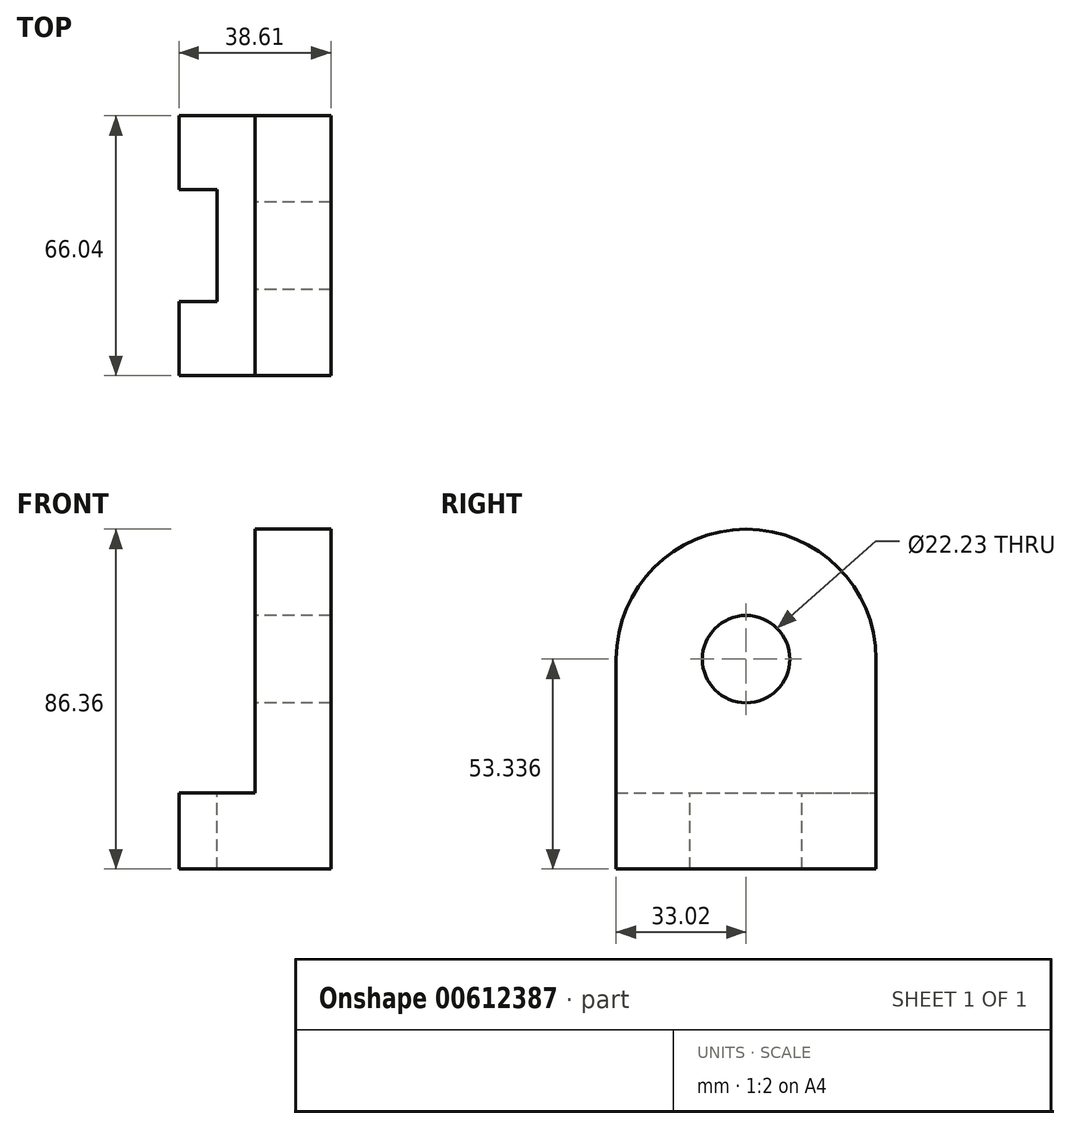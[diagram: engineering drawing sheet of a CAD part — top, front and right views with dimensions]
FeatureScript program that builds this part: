
annotation { "Feature Type Name" : "Feature", "Feature Type Description" : "" }
export const myFeature = defineFeature(function(context is Context, id is Id, definition is map)
    precondition{}
    {
        {
            var Q0;
            Q0=qCreatedBy(makeId("Front.planeOp"),FACE);
            var sketch = newSketch(context, id + "F0", { "sketchPlane" : qUnion([Q0])});
            skLineSegment(sketch, "E0", {"start": v(0, 0) * mm, "end": v(0, -19.3) * mm});
            skLineSegment(sketch, "E1", {"start": v(0, -19.3) * mm, "end": v(38.6, -19.3) * mm});
            skLineSegment(sketch, "E2", {"start": v(38.6, -19.3) * mm, "end": v(38.6, 67.06) * mm});
            skLineSegment(sketch, "E3", {"start": v(38.6, 67.06) * mm, "end": v(19.3, 67.06) * mm});
            skLineSegment(sketch, "E4", {"start": v(19.3, 67.06) * mm, "end": v(19.3, 0) * mm});
            skLineSegment(sketch, "E5", {"start": v(19.3, 0) * mm, "end": v(0, 0) * mm});
            skSolve(sketch);
        }
        {
            var Q0;
            Q0=makeQuery(id+"F0.imprint","IMPRINT",FACE,{"disambiguationData":[TD([[makeQuery(id+"F0.imprint","IMPRINT",EDGE,{"derivedFrom":sQuery(id+"F0.wireOp",EDGE,"E0")}),1.0]])]});
            extrude(context, id + "F1", {"entities" : qUnion([Q0]), "depth" : 66.04 * mm, "offsetDistance" : 25.4 * mm});
        }
        {
            var Q0;
            Q0=makeQuery(id+"F1.opExtrude","CAP_EDGE",EDGE,{"disambiguationData":[OSD([sQuery(id+"F0.wireOp",EDGE,"E3")])],"isStart":true});
            var Q1;
            Q1=makeQuery(id+"F1.opExtrude","CAP_EDGE",EDGE,{"disambiguationData":[OSD([sQuery(id+"F0.wireOp",EDGE,"E3")])],"isStart":false});
            fillet(context, id + "F2", {"entities" : qUnion([Q0, Q1]), "radius" : 33.02 * mm, "tangentPropagation" : true, "allowEdgeOverflow" : false});
        }
        {
            var Q0;
            Q0=makeQuery(id+"F1.opExtrude","SWEPT_FACE",FACE,{"disambiguationData":[OSD([sQuery(id+"F0.wireOp",EDGE,"E4")])]});
            var sketch = newSketch(context, id + "F3", { "sketchPlane" : qUnion([Q0])});
            skCircle(sketch, "E6", {"center": v(33.02, 34.04) * mm, "radius": 11.11 * mm});
            skSolve(sketch);
        }
        {
            var Q0;
            Q0=sQuery(id+"F3.wireOp",VERTEX,"E6.center");
            var Q1;
            Q1=makeQuery(id+"F1.opExtrude","SWEPT_BODY",BODY,{"disambiguationData":[OSD([sQuery(id+"F0.wireOp",EDGE,"E0"),sQuery(id+"F0.wireOp",EDGE,"E1"),sQuery(id+"F0.wireOp",EDGE,"E2"),sQuery(id+"F0.wireOp",EDGE,"E3"),sQuery(id+"F0.wireOp",EDGE,"E4"),sQuery(id+"F0.wireOp",EDGE,"E5")])]});
            hole(context, id + "F4", {"style" : HoleStyle.SIMPLE, "endStyle" : HoleEndStyle.BLIND, "holeDiameter" : 22.22 * mm, "majorDiameter" : 6.35 * mm, "holeDepth" : 50.8 * mm, "isTappedThrough" : true, "tappedDepth" : 12.7 * mm, "tapClearance" : 3, "locations" : qUnion([Q0]), "scope" : qUnion([Q1])});
        }
        {
            var Q0;
            Q0=makeQuery(id+"F1.opExtrude","SWEPT_FACE",FACE,{"disambiguationData":[OSD([sQuery(id+"F0.wireOp",EDGE,"E5")])]});
            var sketch = newSketch(context, id + "F5", { "sketchPlane" : qUnion([Q0])});
            skLineSegment(sketch, "E7", {"start": v(0, -47.24) * mm, "end": v(9.65, -47.24) * mm});
            skLineSegment(sketch, "E8", {"start": v(9.65, -47.24) * mm, "end": v(9.65, -18.8) * mm});
            skLineSegment(sketch, "E9", {"start": v(9.65, -18.8) * mm, "end": v(0, -18.8) * mm});
            skPoint(sketch, "E10.endSnap0", {"position": v(9.65, -66.04) * mm});
            skSolve(sketch);
        }
        {
            var Q0;
            {var subQ0=sQuery(id+"F5.wireOp",EDGE,"E7");Q0=makeQuery(id+"F5.imprint","IMPRINT",FACE,{"disambiguationData":[TD([[makeQuery(id+"F5.imprint","IMPRINT",EDGE,{"derivedFrom":subQ0}),1.0]])]});}
            extrude(context, id + "F6", {"entities" : qUnion([Q0]), "operationType" : NewBodyOperationType.REMOVE, "oppositeDirection" : true, "depth" : 25.4 * mm, "offsetDistance" : 25.4 * mm});
        }
    });
